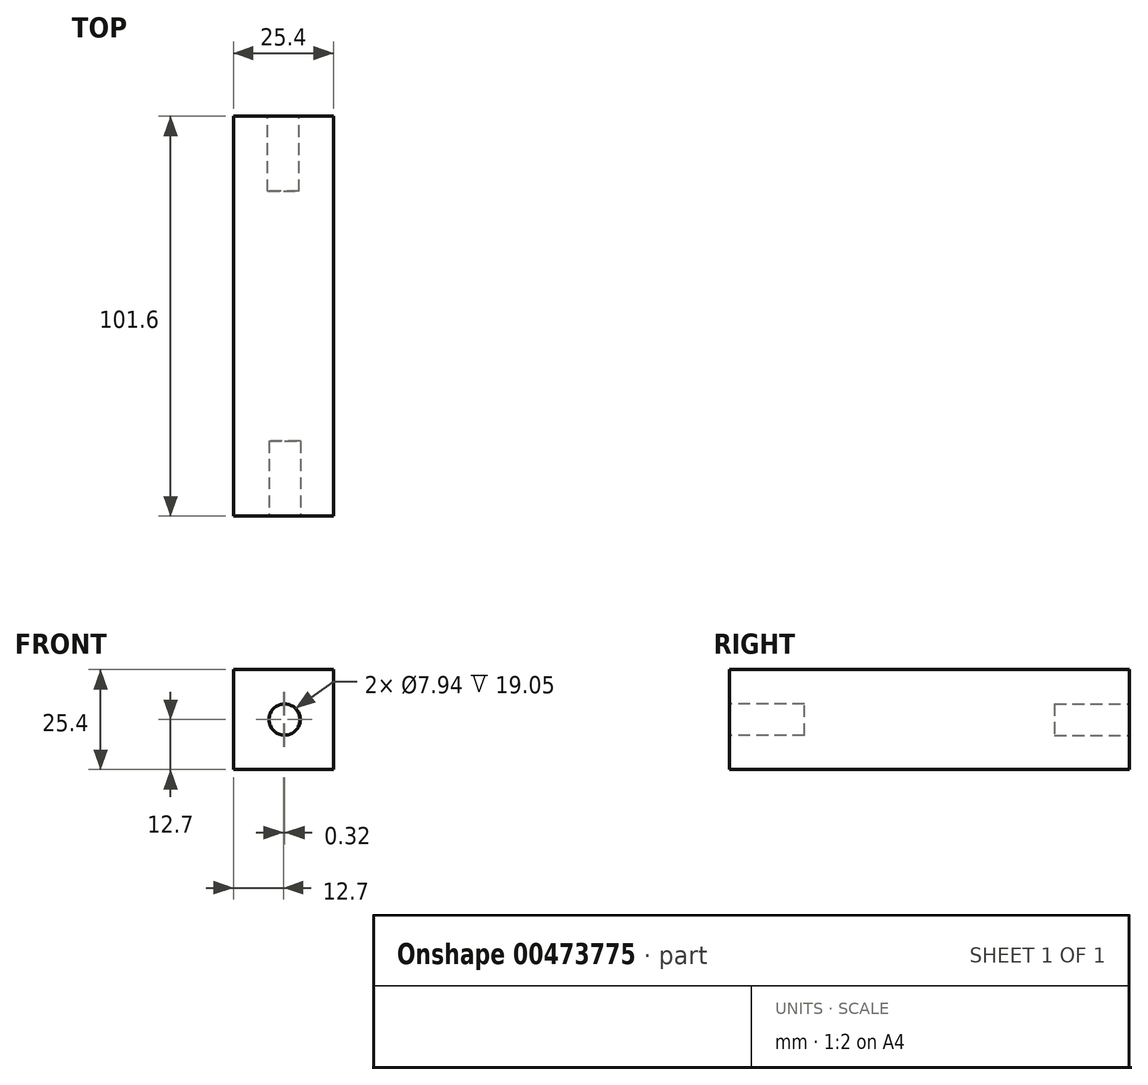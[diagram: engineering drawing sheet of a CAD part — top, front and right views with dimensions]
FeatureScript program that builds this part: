
annotation { "Feature Type Name" : "Feature", "Feature Type Description" : "" }
export const myFeature = defineFeature(function(context is Context, id is Id, definition is map)
    precondition{}
    {
        {
            var Q0;
            Q0=qCreatedBy(makeId("Right.planeOp"),FACE);
            var sketch = newSketch(context, id + "F0", { "sketchPlane" : qUnion([Q0])});
            skLineSegment(sketch, "E0.bottom", {"start": v(0, 0) * mm, "end": v(101.6, 0) * mm});
            skLineSegment(sketch, "E0.top", {"start": v(0, 25.4) * mm, "end": v(101.6, 25.4) * mm});
            skLineSegment(sketch, "E0.left", {"start": v(0, 0) * mm, "end": v(0, 25.4) * mm});
            skLineSegment(sketch, "E0.right", {"start": v(101.6, 0) * mm, "end": v(101.6, 25.4) * mm});
            skSolve(sketch);
        }
        {
            var Q0;
            Q0 = qSketchRegion(id + "F0", true);
            extrude(context, id + "F1", {"entities" : qUnion([Q0]), "depth" : 25.4 * mm});
        }
        {
            var Q0;
            Q0=makeQuery(id+"F1.opExtrude","SWEPT_FACE",FACE,{"disambiguationData":[OSD([sQuery(id+"F0.wireOp",EDGE,"E0.right")])]});
            var sketch = newSketch(context, id + "F2", { "sketchPlane" : qUnion([Q0])});
            skLineSegment(sketch, "E1", {"start": v(-12.7, 0) * mm, "end": v(-12.7, 25.4) * mm, "construction": true});
            skCircle(sketch, "E2", {"center": v(-12.7, 12.7) * mm, "radius": 3.97 * mm});
            skSolve(sketch);
        }
        {
            var Q0;
            Q0 = qSketchRegion(id + "F2", true);
            extrude(context, id + "F3", {"entities" : qUnion([Q0]), "operationType" : NewBodyOperationType.REMOVE, "oppositeDirection" : true, "depth" : 19.05 * mm});
        }
        {
            var Q0;
            Q0=makeQuery(id+"F1.opExtrude","SWEPT_FACE",FACE,{"disambiguationData":[OSD([sQuery(id+"F0.wireOp",EDGE,"E0.left")])]});
            var sketch = newSketch(context, id + "F4", { "sketchPlane" : qUnion([Q0])});
            skLineSegment(sketch, "E3", {"start": v(13.34, 0) * mm, "end": v(12.7, 25.4) * mm, "construction": true});
            skCircle(sketch, "E4", {"center": v(13.02, 12.7) * mm, "radius": 3.97 * mm});
            skSolve(sketch);
        }
        {
            var Q0;
            Q0 = qSketchRegion(id + "F4", true);
            extrude(context, id + "F5", {"entities" : qUnion([Q0]), "operationType" : NewBodyOperationType.REMOVE, "oppositeDirection" : true, "depth" : 19.05 * mm});
        }
    });
